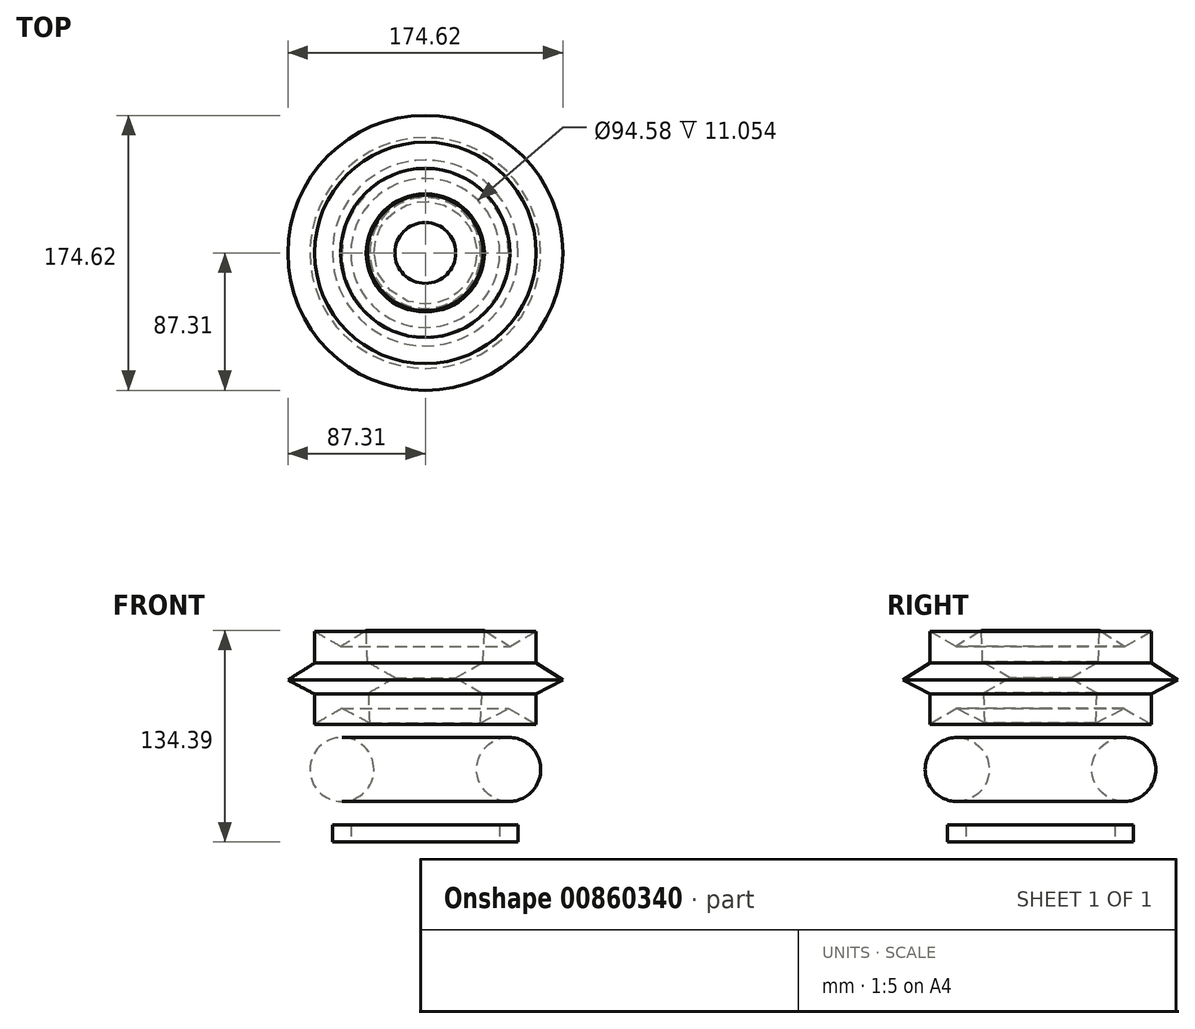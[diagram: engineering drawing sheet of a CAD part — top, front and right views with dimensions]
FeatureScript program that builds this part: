
annotation { "Feature Type Name" : "Feature", "Feature Type Description" : "" }
export const myFeature = defineFeature(function(context is Context, id is Id, definition is map)
    precondition{}
    {
        {
            var Q0;
            Q0=qCreatedBy(makeId("Front.planeOp"),FACE);
            var sketch = newSketch(context, id + "F0", { "sketchPlane" : qUnion([Q0])});
            skLineSegment(sketch, "E0", {"start": v(0, 0) * mm, "end": v(0, 164.33) * mm, "construction": true});
            skCircle(sketch, "E1", {"center": v(113.37, 138.2) * mm, "radius": 96.2 * mm});
            skSolve(sketch);
        }
        {
            var Q0;
            Q0=makeQuery(id+"F0.imprint","IMPRINT",FACE,{"disambiguationData":[TD([[makeQuery(id+"F0.imprint","IMPRINT",EDGE,{"derivedFrom":sQuery(id+"F0.wireOp",EDGE,"E1")}),1.0]])]});
            var Q1;
            Q1=sQuery(id+"F0.wireOp",EDGE,"E0");
            revolve(context, id + "F1", {"surfaceOperationType" : NewSurfaceOperationType.NEW, "entities" : qUnion([Q0]), "axis" : qUnion([Q1]), "revolveType" : RevolveType.FULL});
        }
        {
            var Q0;
            Q0=qCreatedBy(makeId("Front.planeOp"),FACE);
            var sketch = newSketch(context, id + "F2", { "sketchPlane" : qUnion([Q0])});
            skCircle(sketch, "E2", {"center": v(165.68, 54.87) * mm, "radius": 37.53 * mm});
            skCircle(sketch, "E3", {"center": v(-158.46, 50.24) * mm, "radius": 37.44 * mm});
            skSolve(sketch);
        }
        {
            var Q0;
            Q0 = qSketchRegion(id + "F2", true);
            extrude(context, id + "F3", {"entities" : qUnion([Q0]), "operationType" : NewBodyOperationType.ADD, "depth" : 215.9 * mm, "offsetDistance" : 25.4 * mm});
        }
        {
            var Q0;
            Q0=makeQuery(id+"F1.opRevolve","SWEPT_BODY",BODY,{"disambiguationData":[OSD([sQuery(id+"F0.wireOp",EDGE,"E1")])]});
            deleteBodies(context, id + "F4", {"entities" : qUnion([Q0])});
        }
        {
            var Q0;
            Q0=qCreatedBy(makeId("Front.planeOp"),FACE);
            var sketch = newSketch(context, id + "F5", { "sketchPlane" : qUnion([Q0])});
            skLineSegment(sketch, "E4", {"start": v(0, 0) * mm, "end": v(0, 71.22) * mm, "construction": true});
            skCircle(sketch, "E5", {"center": v(52.96, 35.04) * mm, "radius": 20.33 * mm});
            skLineSegment(sketch, "E6.bottom", {"start": v(47.29, -11.05) * mm, "end": v(59, -11.05) * mm});
            skLineSegment(sketch, "E6.top", {"start": v(47.29, 0) * mm, "end": v(59, 0) * mm});
            skLineSegment(sketch, "E6.left", {"start": v(47.29, 0) * mm, "end": v(47.29, -11.05) * mm});
            skLineSegment(sketch, "E6.right", {"start": v(59, 0) * mm, "end": v(59, -11.05) * mm});
            skCircle(sketch, "E7.cCircle", {"center": v(53.33, 93.23) * mm, "radius": 17 * mm, "construction": true});
            skLineSegment(sketch, "E7.0", {"start": v(70.34, 122.68) * mm, "end": v(70.34, 63.78) * mm});
            skLineSegment(sketch, "E7.1", {"start": v(70.34, 63.78) * mm, "end": v(19.33, 93.23) * mm});
            skLineSegment(sketch, "E7.2", {"start": v(19.33, 93.23) * mm, "end": v(70.34, 122.68) * mm});
            skPoint(sketch, "E7.0.midPoint", {"position": v(70.34, 93.23) * mm});
            skLineSegment(sketch, "E8.0", {"start": v(37.51, 123.34) * mm, "end": v(87.31, 91.88) * mm});
            skLineSegment(sketch, "E8.1", {"start": v(87.31, 91.88) * mm, "end": v(35.18, 64.48) * mm});
            skLineSegment(sketch, "E8.2", {"start": v(35.18, 64.48) * mm, "end": v(37.51, 123.34) * mm});
            skPoint(sketch, "E8.0.midPoint", {"position": v(62.41, 107.6) * mm});
            skSolve(sketch);
        }
        {
            var Q0;
            Q0 = qSketchRegion(id + "F5", true);
            var Q1;
            Q1=sQuery(id+"F5.wireOp",EDGE,"E4");
            revolve(context, id + "F6", {"surfaceOperationType" : NewSurfaceOperationType.NEW, "entities" : qUnion([Q0]), "axis" : qUnion([Q1]), "revolveType" : RevolveType.FULL});
        }
    });
